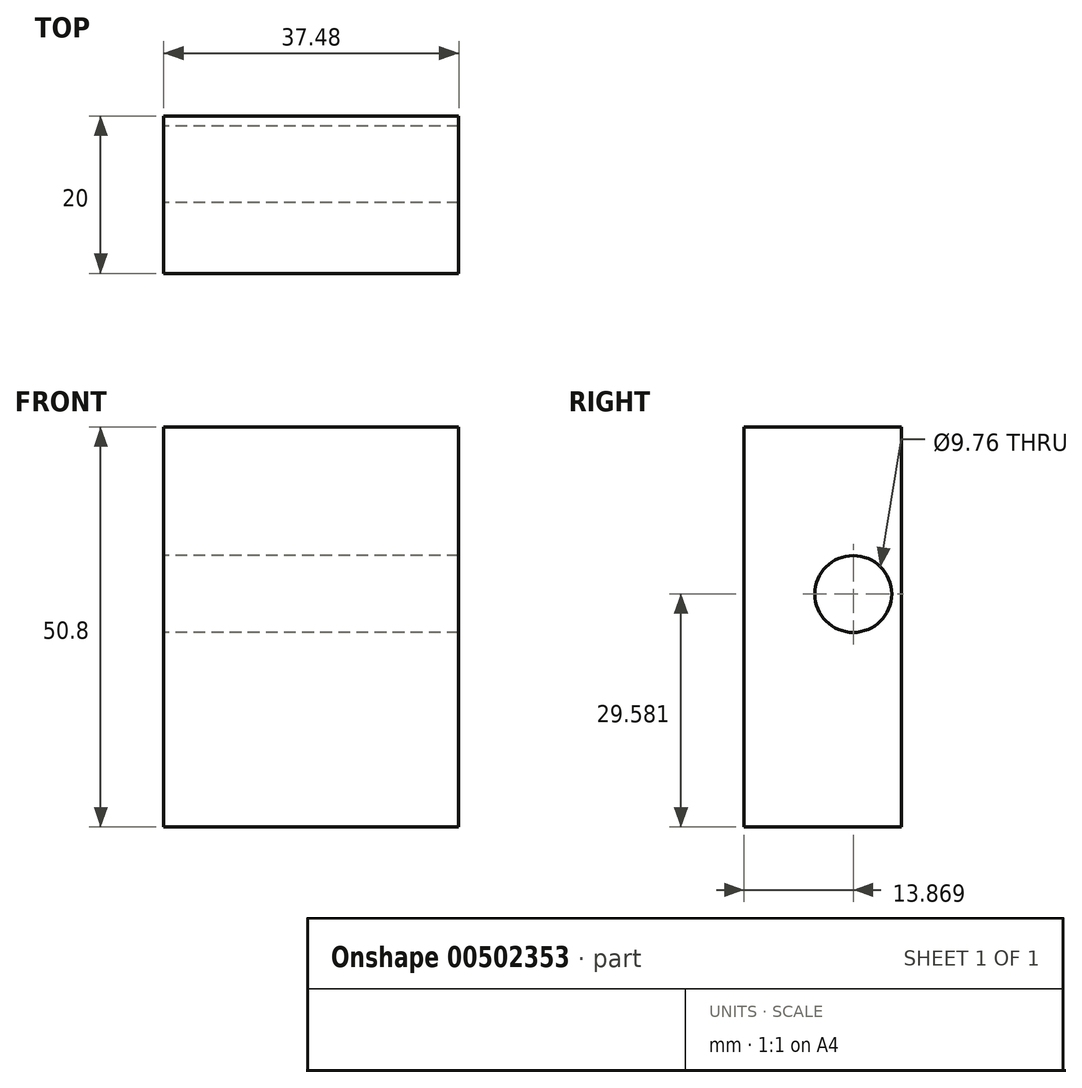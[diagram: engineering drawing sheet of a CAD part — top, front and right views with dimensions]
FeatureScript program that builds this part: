
annotation { "Feature Type Name" : "Feature", "Feature Type Description" : "" }
export const myFeature = defineFeature(function(context is Context, id is Id, definition is map)
    precondition{}
    {
        {
            var Q0;
            Q0=qCreatedBy(makeId("Top.planeOp"),FACE);
            var sketch = newSketch(context, id + "F0", { "sketchPlane" : qUnion([Q0])});
            skLineSegment(sketch, "E0", {"start": v(-34.6, 36.68) * mm, "end": v(-4.89, 4.02) * mm});
            skLineSegment(sketch, "E1.bottom", {"start": v(-17.45, 44.99) * mm, "end": v(20.03, 44.99) * mm});
            skLineSegment(sketch, "E1.top", {"start": v(-17.45, 24.99) * mm, "end": v(20.03, 24.99) * mm});
            skLineSegment(sketch, "E1.left", {"start": v(-17.45, 44.99) * mm, "end": v(-17.45, 24.99) * mm});
            skLineSegment(sketch, "E1.right", {"start": v(20.03, 44.99) * mm, "end": v(20.03, 24.99) * mm});
            skSolve(sketch);
        }
        {
            var Q0;
            Q0 = qSketchRegion(id + "F0", true);
            extrude(context, id + "F1", {"entities" : qUnion([Q0]), "depth" : 50.8 * mm});
        }
        {
            var Q0;
            Q0=makeQuery(id+"F1.opExtrude","SWEPT_FACE",FACE,{"disambiguationData":[OSD([sQuery(id+"F0.wireOp",EDGE,"E1.left")])]});
            var sketch = newSketch(context, id + "F2", { "sketchPlane" : qUnion([Q0])});
            skCircle(sketch, "E2", {"center": v(-38.86, 29.58) * mm, "radius": 4.88 * mm});
            skSolve(sketch);
        }
        {
            var Q0;
            Q0=makeQuery(id+"F2.imprint","IMPRINT",FACE,{"disambiguationData":[TD([[makeQuery(id+"F2.imprint","IMPRINT",EDGE,{"derivedFrom":sQuery(id+"F2.wireOp",EDGE,"E2")}),1.0]])]});
            var Q1;
            Q1=sQuery(id+"F2.wireOp",EDGE,"E2");
            extrude(context, id + "F3", {"entities" : qUnion([Q0]), "operationType" : NewBodyOperationType.REMOVE, "surfaceEntities" : qUnion([Q1]), "oppositeDirection" : true, "depth" : 254 * mm});
        }
    });
